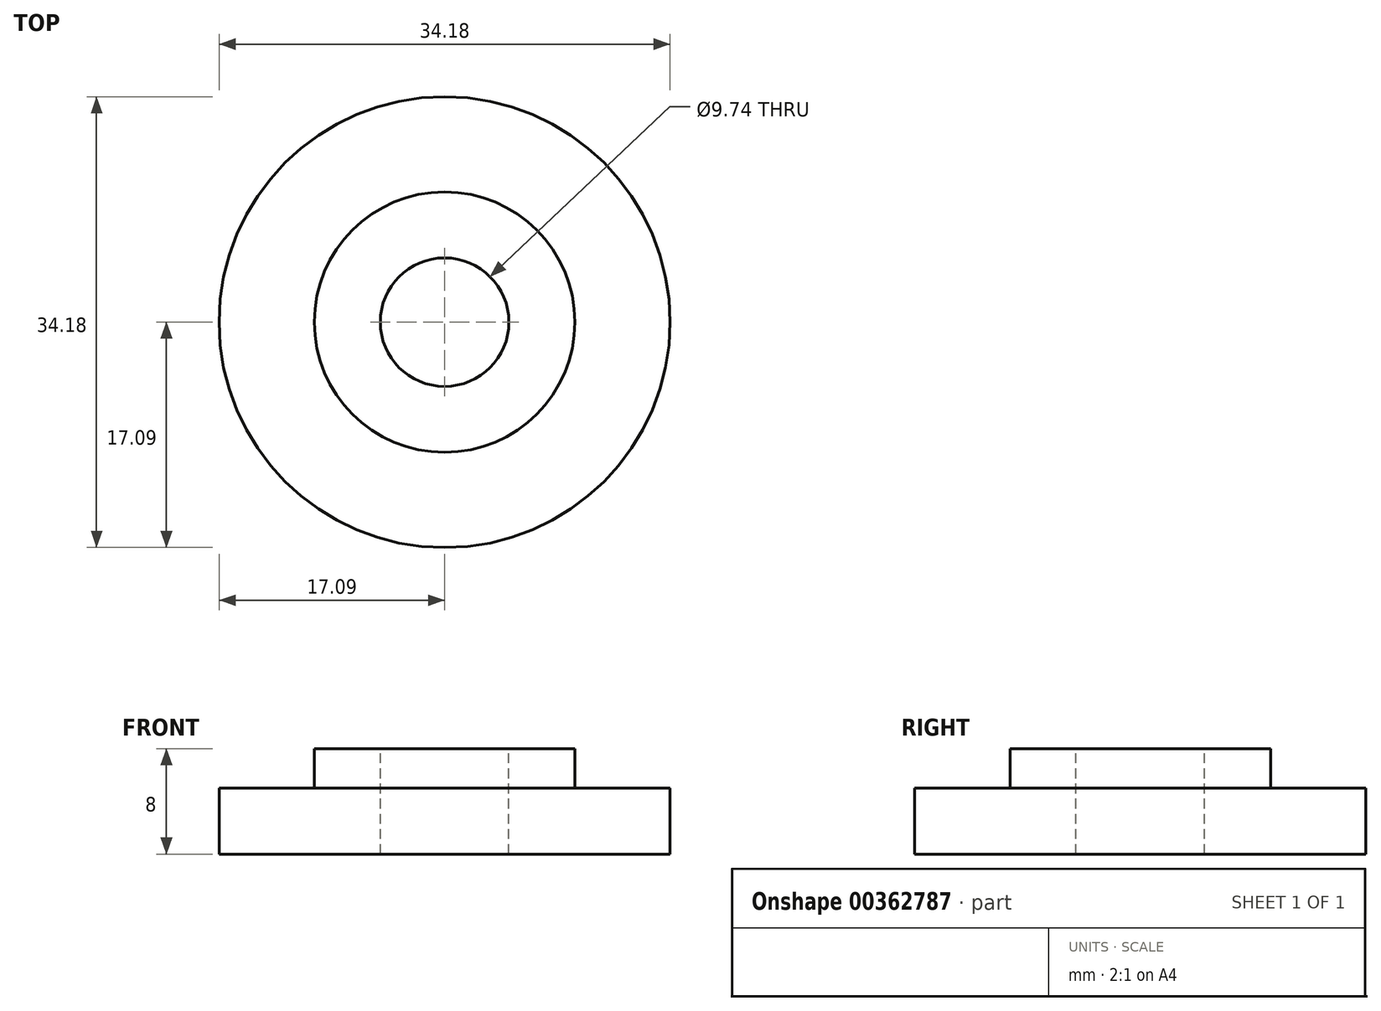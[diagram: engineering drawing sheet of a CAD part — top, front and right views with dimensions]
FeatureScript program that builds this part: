
annotation { "Feature Type Name" : "Feature", "Feature Type Description" : "" }
export const myFeature = defineFeature(function(context is Context, id is Id, definition is map)
    precondition{}
    {
        {
            var Q0;
            Q0=qCreatedBy(makeId("Top.planeOp"),FACE);
            var sketch = newSketch(context, id + "F0", { "sketchPlane" : qUnion([Q0])});
            skCircle(sketch, "E0", {"center": v(0, 0) * mm, "radius": 17.1 * mm});
            skCircle(sketch, "E1", {"center": v(0, 0) * mm, "radius": 4.88 * mm});
            skCircle(sketch, "E2", {"center": v(0, 0) * mm, "radius": 9.88 * mm});
            skSolve(sketch);
        }
        {
            var Q0;
            Q0=makeQuery(id+"F0.imprint","IMPRINT",FACE,{"disambiguationData":[TD([[makeQuery(id+"F0.imprint","IMPRINT",EDGE,{"derivedFrom":sQuery(id+"F0.wireOp",EDGE,"E1")}),1.0]])]});
            var Q1;
            Q1=makeQuery(id+"F0.imprint","IMPRINT",FACE,{"disambiguationData":[TD([[makeQuery(id+"F0.imprint","IMPRINT",EDGE,{"derivedFrom":sQuery(id+"F0.wireOp",EDGE,"E1")}),-1.0]])]});
            var Q2;
            Q2=sQuery(id+"F0.wireOp",EDGE,"E2");
            var Q3;
            Q3=sQuery(id+"F0.wireOp",EDGE,"E1");
            extrude(context, id + "F1", {"entities" : qUnion([Q0, Q1]), "surfaceEntities" : qUnion([Q2, Q3]), "depth" : 8 * mm});
        }
        {
            var Q0;
            Q0 = qSketchRegion(id + "F0", true);
            extrude(context, id + "F2", {"entities" : qUnion([Q0]), "operationType" : NewBodyOperationType.ADD, "depth" : 5 * mm});
        }
        {
            var Q0;
            Q0=makeQuery(id+"F1.opExtrude","CAP_FACE",FACE,{"disambiguationData":[OSD([sQuery(id+"F0.wireOp",EDGE,"E2")])],"isStart":false});
            var sketch = newSketch(context, id + "F3", { "sketchPlane" : qUnion([Q0])});
            skCircle(sketch, "E3", {"center": v(0, 0) * mm, "radius": 4.87 * mm});
            skSolve(sketch);
        }
        {
            var Q0;
            Q0 = qSketchRegion(id + "F3", true);
            extrude(context, id + "F4", {"entities" : qUnion([Q0]), "operationType" : NewBodyOperationType.REMOVE, "oppositeDirection" : true, "depth" : 25 * mm});
        }
    });
